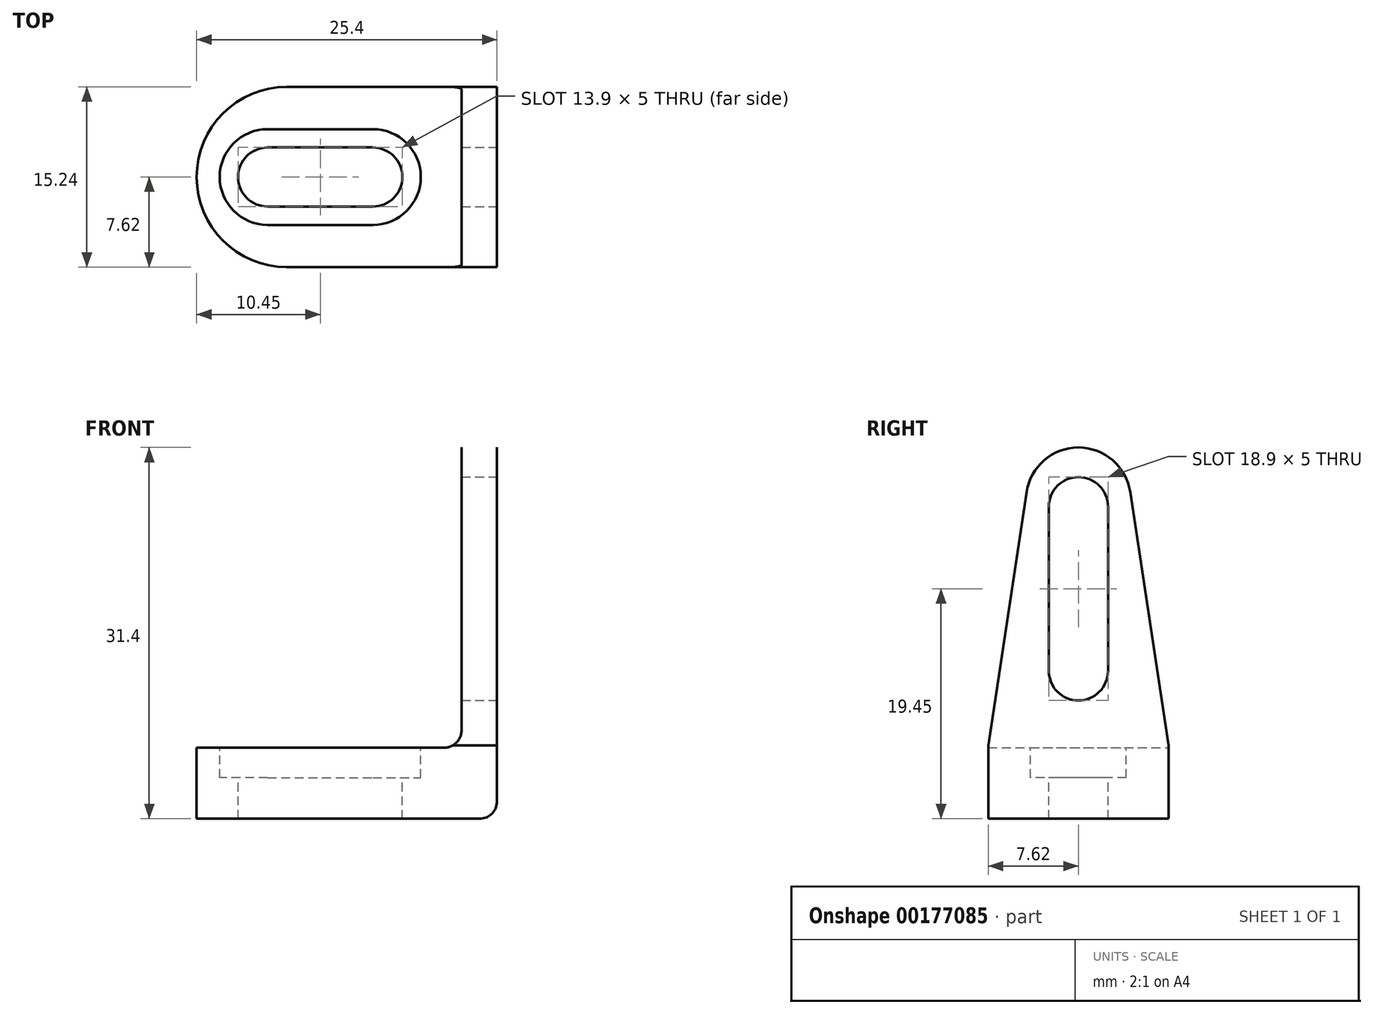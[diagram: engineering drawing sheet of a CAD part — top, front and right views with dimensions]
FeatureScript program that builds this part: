
annotation { "Feature Type Name" : "Feature", "Feature Type Description" : "" }
export const myFeature = defineFeature(function(context is Context, id is Id, definition is map)
    precondition{}
    {
        {
            var Q0;
            Q0=qCreatedBy(makeId("Front.planeOp"),FACE);
            var sketch = newSketch(context, id + "F0", { "sketchPlane" : qUnion([Q0])});
            skLineSegment(sketch, "E0.top", {"start": v(-4.5, 3) * mm, "end": v(-25.4, 3) * mm});
            skLineSegment(sketch, "E1.top", {"start": v(-1.5, 28.4) * mm, "end": v(-1.5, 28.4) * mm});
            skLineSegment(sketch, "E1.left", {"start": v(0, -1.5) * mm, "end": v(0, 28.4) * mm});
            skLineSegment(sketch, "E1.right", {"start": v(-3, 4.5) * mm, "end": v(-3, 28.4) * mm});
            skPoint(sketch, "E2.visualSharp", {"position": v(-3, 3) * mm});
            skArc(sketch, "E2.filletArc", {"start": v(-4.5, 3) * mm, "mid": v(-3.44, 3.44) * mm, "end": v(-3, 4.5) * mm});
            skPoint(sketch, "E3.visualSharp", {"position": v(0, 0) * mm});
            skPoint(sketch, "E4.visualSharp", {"position": v(-3, 28.4) * mm});
            skPoint(sketch, "E5.visualSharp", {"position": v(0, 28.4) * mm});
            skPoint(sketch, "E6.visualSharp", {"position": v(-52.3, 3) * mm});
            skLineSegment(sketch, "E7", {"start": v(-25.4, -3) * mm, "end": v(-1.5, -3) * mm});
            skPoint(sketch, "E8.visualSharp", {"position": v(-52.3, -3) * mm});
            skPoint(sketch, "E9.visualSharp", {"position": v(0, -3) * mm});
            skArc(sketch, "E9.filletArc", {"start": v(-1.5, -3) * mm, "mid": v(-0.44, -2.56) * mm, "end": v(0, -1.5) * mm});
            skLineSegment(sketch, "E10", {"start": v(-3, 28.4) * mm, "end": v(0, 28.4) * mm});
            skLineSegment(sketch, "E11.trimOffspring", {"start": v(-25.4, 3) * mm, "end": v(-25.4, -3) * mm});
            skSolve(sketch);
        }
        {
            var Q0;
            Q0=qSketchRegion(id+"F0",true);
            extrude(context, id + "F1", {"entities" : qUnion([Q0]), "depth" : 15.24 * mm});
        }
        {
            var Q0;
            Q0=makeQuery(id+"F1.opExtrude","SWEPT_FACE",FACE,{"disambiguationData":[OSD([sQuery(id+"F0.wireOp",EDGE,"E1.left")])]});
            var sketch = newSketch(context, id + "F2", { "sketchPlane" : qUnion([Q0])});
            skLineSegment(sketch, "E12", {"start": v(-7.62, 23.4) * mm, "end": v(-7.62, 9.5) * mm});
            skArc(sketch, "E13.0.startCap", {"start": v(-10.12, 23.4) * mm, "mid": v(-7.62, 25.9) * mm, "end": v(-5.12, 23.4) * mm});
            skArc(sketch, "E13.0.endCap", {"start": v(-5.12, 9.5) * mm, "mid": v(-7.62, 7) * mm, "end": v(-10.12, 9.5) * mm});
            skLineSegment(sketch, "E13.0.left", {"start": v(-5.12, 23.4) * mm, "end": v(-5.12, 9.5) * mm});
            skLineSegment(sketch, "E13.0.right", {"start": v(-10.12, 23.4) * mm, "end": v(-10.12, 9.5) * mm});
            skSolve(sketch);
        }
        {
            var Q0;
            Q0=qSketchRegion(id+"F2",true);
            extrude(context, id + "F3", {"entities" : qUnion([Q0]), "operationType" : NewBodyOperationType.REMOVE, "endBound" : BoundingType.UP_TO_NEXT, "oppositeDirection" : true, "depth" : 25.4 * mm});
        }
        {
            var Q0;
            Q0=makeQuery(id+"F1.opExtrude","SWEPT_FACE",FACE,{"disambiguationData":[OSD([sQuery(id+"F0.wireOp",EDGE,"E0.top")])]});
            var sketch = newSketch(context, id + "F4", { "sketchPlane" : qUnion([Q0])});
            skLineSegment(sketch, "E14", {"start": v(-19.4, -7.62) * mm, "end": v(-10.5, -7.62) * mm});
            skPoint(sketch, "E14.startSnap0", {"position": v(-4.5, -7.62) * mm});
            skPoint(sketch, "E14.endSnap0", {"position": v(-4.5, -7.62) * mm});
            skArc(sketch, "E15.0.startCap", {"start": v(-19.4, -10.12) * mm, "mid": v(-21.9, -7.62) * mm, "end": v(-19.4, -5.12) * mm});
            skArc(sketch, "E15.0.endCap", {"start": v(-10.5, -5.12) * mm, "mid": v(-8, -7.62) * mm, "end": v(-10.5, -10.12) * mm});
            skLineSegment(sketch, "E15.0.left", {"start": v(-19.4, -5.12) * mm, "end": v(-10.5, -5.12) * mm});
            skLineSegment(sketch, "E15.0.right", {"start": v(-19.4, -10.12) * mm, "end": v(-10.5, -10.12) * mm});
            skArc(sketch, "E16.0.startCap", {"start": v(-19.4, -11.67) * mm, "mid": v(-23.45, -7.62) * mm, "end": v(-19.4, -3.57) * mm});
            skArc(sketch, "E16.0.endCap", {"start": v(-10.5, -3.57) * mm, "mid": v(-6.45, -7.62) * mm, "end": v(-10.5, -11.67) * mm});
            skLineSegment(sketch, "E16.0.left", {"start": v(-19.4, -3.57) * mm, "end": v(-10.5, -3.57) * mm});
            skLineSegment(sketch, "E16.0.right", {"start": v(-19.4, -11.67) * mm, "end": v(-10.5, -11.67) * mm});
            skSolve(sketch);
        }
        {
            var Q0;
            Q0=qSketchRegion(id+"F4",true);
            extrude(context, id + "F5", {"entities" : qUnion([Q0]), "operationType" : NewBodyOperationType.REMOVE, "oppositeDirection" : true, "depth" : 2.54 * mm});
        }
        {
            var Q0;
            Q0=makeQuery(id+"F5.boolean.opBoolean","SPLIT",FACE,{"disambiguationData":[TD([makeQuery(id+"F5.opExtrude","SWEPT_FACE",FACE,{"disambiguationData":[OSD([sQuery(id+"F4.wireOp",EDGE,"E15.0.startCap")])]})])],"derivedFrom":makeQuery(id+"F1.opExtrude","SWEPT_FACE",FACE,{"disambiguationData":[OSD([sQuery(id+"F0.wireOp",EDGE,"E0.top")])]})});
            extrude(context, id + "F6", {"entities" : qUnion([Q0]), "operationType" : NewBodyOperationType.REMOVE, "endBound" : BoundingType.UP_TO_NEXT, "oppositeDirection" : true, "depth" : 25.4 * mm});
        }
        {
            var Q0;
            Q0=makeQuery(id+"F1.opExtrude","CAP_EDGE",EDGE,{"disambiguationData":[OSD([sQuery(id+"F0.wireOp",EDGE,"E10")])],"isStart":false});
            var Q1;
            Q1=makeQuery(id+"F1.opExtrude","CAP_EDGE",EDGE,{"disambiguationData":[OSD([sQuery(id+"F0.wireOp",EDGE,"E10")])],"isStart":true});
            chamfer(context, id + "F7", {"entities" : qUnion([Q0, Q1]), "chamferType" : ChamferType.OFFSET_ANGLE, "width" : 3.8 * mm, "oppositeDirection" : false, "angle" : 81.4 * degree, "tangentPropagation" : true});
        }
        {
            var Q0;
            {var subQ0=sQuery(id+"F0.wireOp",EDGE,"E10");Q0=makeQuery(id+"F7.opChamfer","BLEND_EDGE",EDGE,{"blendedFrom":[makeQuery(id+"F1.opExtrude","CAP_EDGE",EDGE,{"disambiguationData":[OSD([subQ0])],"isStart":false}),makeQuery(id+"F1.opExtrude","SWEPT_FACE",FACE,{"disambiguationData":[OSD([subQ0])]})],"blendedInto":[makeQuery(id+"F1.opExtrude","SWEPT_FACE",FACE,{"disambiguationData":[OSD([subQ0])]})]});}
            var Q1;
            {var subQ0=sQuery(id+"F0.wireOp",EDGE,"E10");Q1=makeQuery(id+"F7.opChamfer","BLEND_EDGE",EDGE,{"blendedFrom":[makeQuery(id+"F1.opExtrude","CAP_EDGE",EDGE,{"disambiguationData":[OSD([subQ0])],"isStart":true}),makeQuery(id+"F1.opExtrude","SWEPT_FACE",FACE,{"disambiguationData":[OSD([subQ0])]})],"blendedInto":[makeQuery(id+"F1.opExtrude","SWEPT_FACE",FACE,{"disambiguationData":[OSD([subQ0])]})]});}
            fillet(context, id + "F8", {"entities" : qUnion([Q0, Q1]), "radius" : 4.44 * mm, "tangentPropagation" : true, "allowEdgeOverflow" : false});
        }
        {
            var Q0;
            Q0=makeQuery(id+"F1.opExtrude","CAP_EDGE",EDGE,{"disambiguationData":[OSD([sQuery(id+"F0.wireOp",EDGE,"E11.trimOffspring")])],"isStart":false});
            var Q1;
            Q1=makeQuery(id+"F1.opExtrude","CAP_EDGE",EDGE,{"disambiguationData":[OSD([sQuery(id+"F0.wireOp",EDGE,"E11.trimOffspring")])],"isStart":true});
            fillet(context, id + "F9", {"entities" : qUnion([Q0, Q1]), "radius" : 7.62 * mm, "tangentPropagation" : true, "allowEdgeOverflow" : false});
        }
    });
